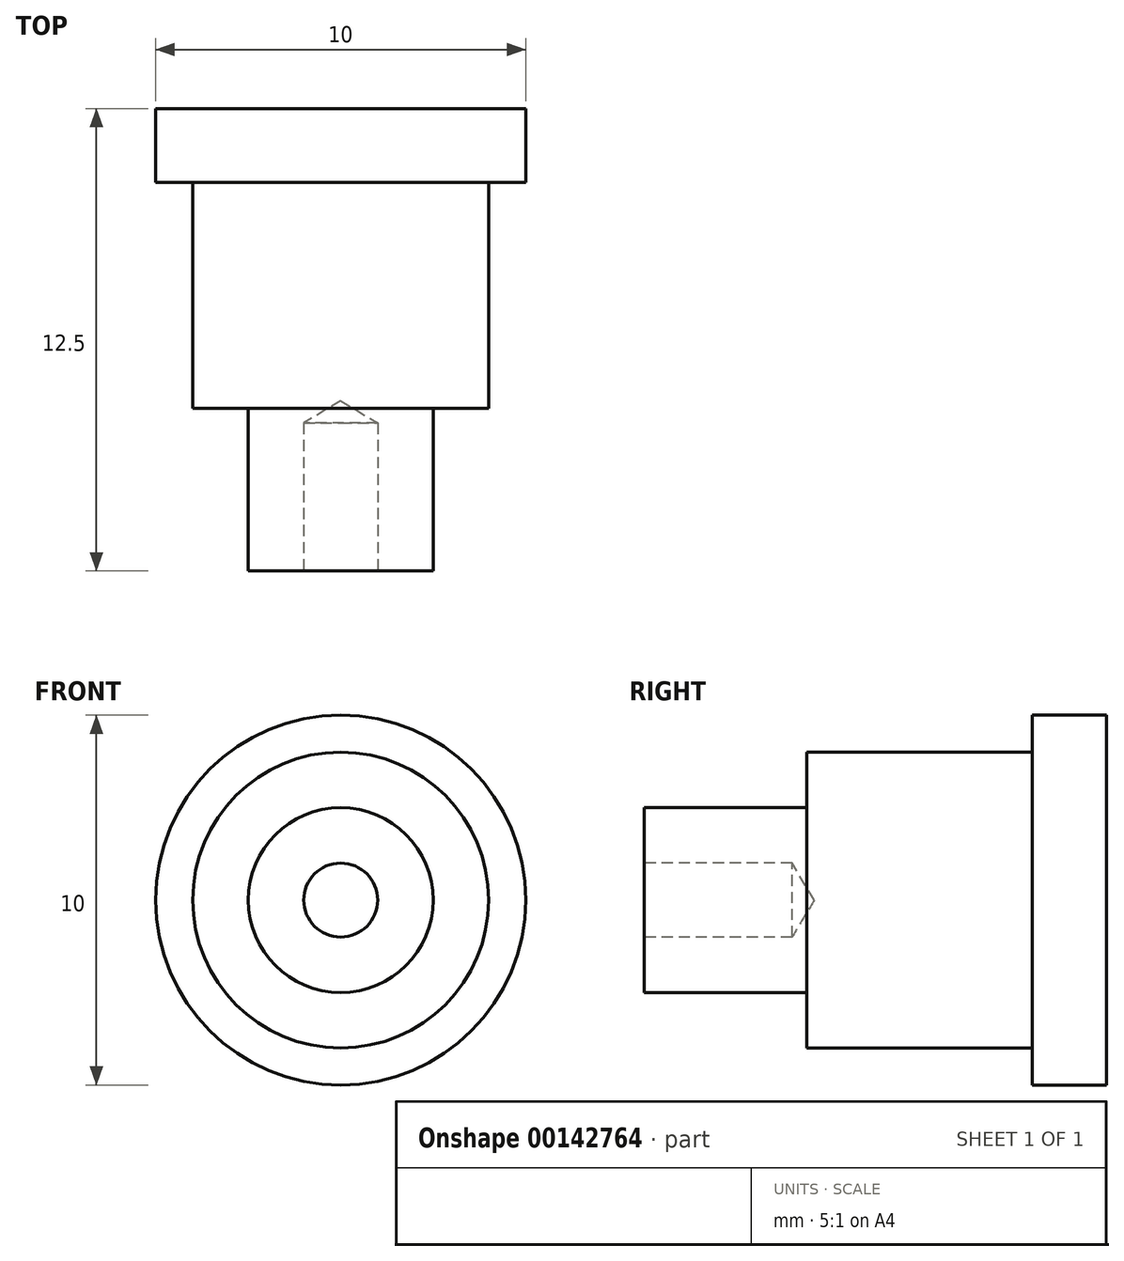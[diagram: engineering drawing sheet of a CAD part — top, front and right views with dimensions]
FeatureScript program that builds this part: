
annotation { "Feature Type Name" : "Feature", "Feature Type Description" : "" }
export const myFeature = defineFeature(function(context is Context, id is Id, definition is map)
    precondition{}
    {
        {
            var Q0;
            Q0=qCreatedBy(makeId("Front.planeOp"),FACE);
            var sketch = newSketch(context, id + "F0", { "sketchPlane" : qUnion([Q0])});
            skCircle(sketch, "E0", {"center": v(0, 0) * mm, "radius": 2.5 * mm});
            skCircle(sketch, "E1", {"center": v(0, 0) * mm, "radius": 1 * mm});
            skCircle(sketch, "E2", {"center": v(0, 0) * mm, "radius": 4 * mm});
            skCircle(sketch, "E3", {"center": v(0, 0) * mm, "radius": 5 * mm});
            skSolve(sketch);
        }
        {
            var Q0;
            Q0=makeQuery(id+"F0.imprint","IMPRINT",FACE,{"disambiguationData":[TD([[makeQuery(id+"F0.imprint","IMPRINT",EDGE,{"derivedFrom":sQuery(id+"F0.wireOp",EDGE,"E2")}),-1.0]])]});
            extrude(context, id + "F1", {"entities" : qUnion([Q0]), "depth" : 2 * mm});
        }
        {
            var Q0;
            Q0=makeQuery(id+"F0.imprint","IMPRINT",FACE,{"disambiguationData":[TD([[makeQuery(id+"F0.imprint","IMPRINT",EDGE,{"derivedFrom":sQuery(id+"F0.wireOp",EDGE,"E0")}),-1.0]])]});
            extrude(context, id + "F2", {"entities" : qUnion([Q0]), "operationType" : NewBodyOperationType.ADD, "depth" : 8.1 * mm});
        }
        {
            var Q0;
            Q0=makeQuery(id+"F0.imprint","IMPRINT",FACE,{"disambiguationData":[TD([[makeQuery(id+"F0.imprint","IMPRINT",EDGE,{"derivedFrom":sQuery(id+"F0.wireOp",EDGE,"E0")}),1.0]])]});
            extrude(context, id + "F3", {"entities" : qUnion([Q0]), "operationType" : NewBodyOperationType.ADD, "depth" : 12.5 * mm});
        }
        {
            var Q0;
            Q0=makeQuery(id+"F0.imprint","IMPRINT",FACE,{"disambiguationData":[TD([[makeQuery(id+"F0.imprint","IMPRINT",EDGE,{"derivedFrom":sQuery(id+"F0.wireOp",EDGE,"E1")}),1.0]])]});
            var Q1;
            Q1=sQuery(id+"F0.wireOp",EDGE,"E1");
            extrude(context, id + "F4", {"entities" : qUnion([Q0]), "operationType" : NewBodyOperationType.ADD, "surfaceEntities" : qUnion([Q1]), "depth" : 12.5 * mm});
        }
        {
            var Q0;
            {var subQ0=sQuery(id+"F0.wireOp",EDGE,"E1");Q0=makeQuery(id+"F4.boolean.opBoolean","MERGE",FACE,{"derivedFrom":[makeQuery(id+"F3.opExtrude","CAP_FACE",FACE,{"disambiguationData":[OSD([sQuery(id+"F0.wireOp",EDGE,"E0"),subQ0])],"isStart":false}),makeQuery(id+"F4.opExtrude","CAP_FACE",FACE,{"disambiguationData":[OSD([subQ0])],"isStart":false})]});}
            var sketch = newSketch(context, id + "F5", { "sketchPlane" : qUnion([Q0])});
            skCircle(sketch, "E4", {"center": v(0, 0) * mm, "radius": 1 * mm});
            skSolve(sketch);
        }
        {
            var Q0;
            Q0=sQuery(id+"F5.wireOp",VERTEX,"E4.center");
            var Q1;
            Q1=makeQuery(id+"F1.opExtrude","SWEPT_BODY",BODY,{"disambiguationData":[OSD([sQuery(id+"F0.wireOp",EDGE,"E2"),sQuery(id+"F0.wireOp",EDGE,"E3")])]});
            hole(context, id + "F6", {"style" : HoleStyle.SIMPLE, "endStyle" : HoleEndStyle.BLIND, "holeDiameter" : 2 * mm, "holeDepth" : 4 * mm, "locations" : qUnion([Q0]), "scope" : qUnion([Q1])});
        }
    });
